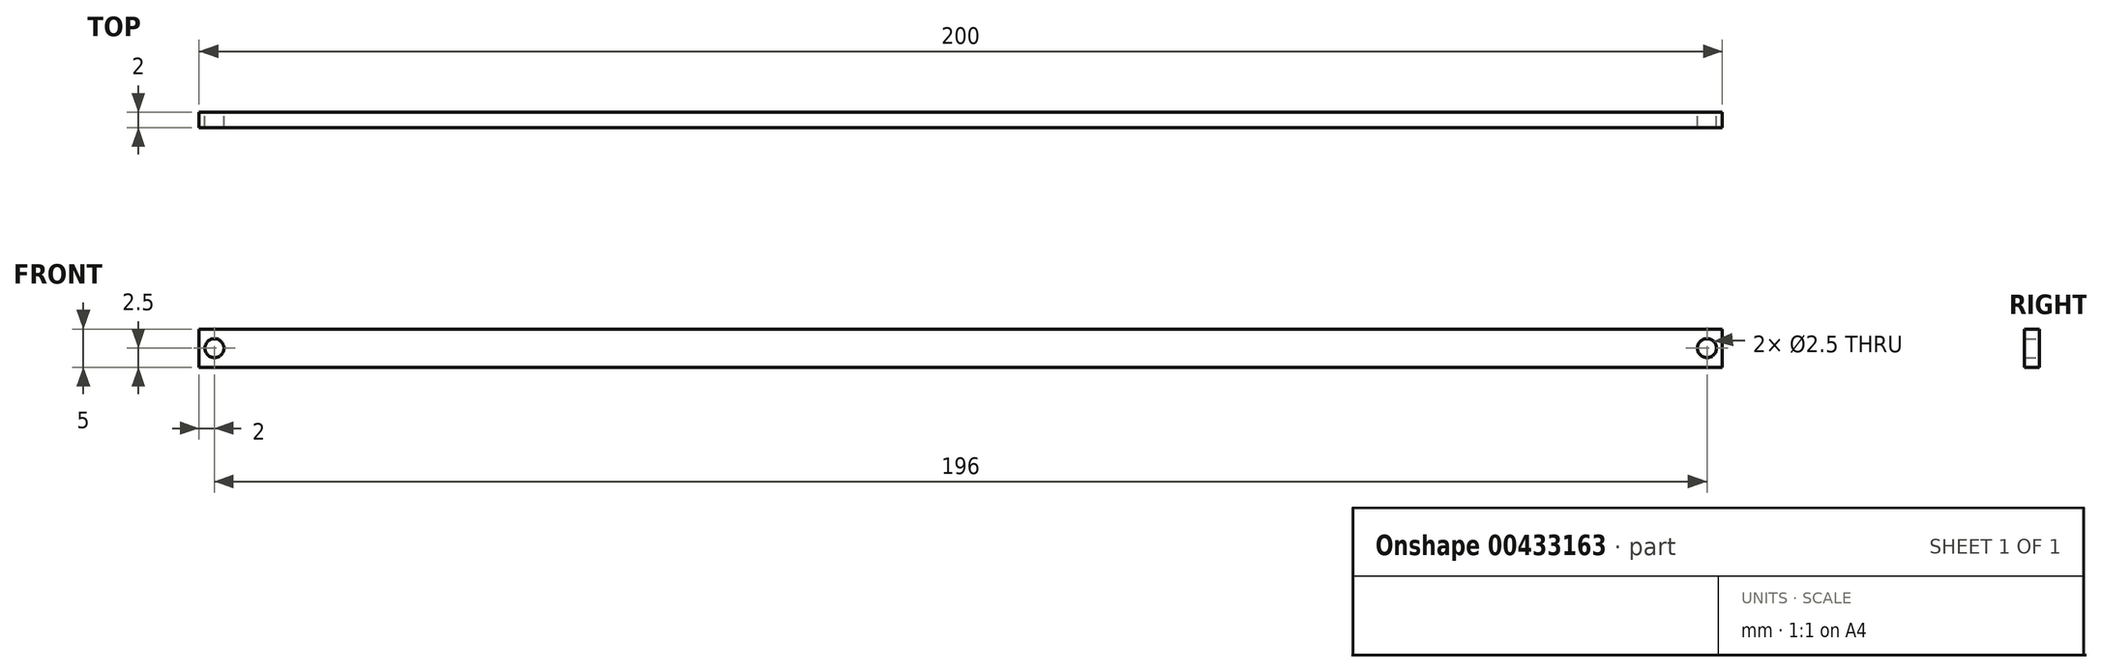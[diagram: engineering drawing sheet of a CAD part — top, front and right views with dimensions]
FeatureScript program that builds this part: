
annotation { "Feature Type Name" : "Feature", "Feature Type Description" : "" }
export const myFeature = defineFeature(function(context is Context, id is Id, definition is map)
    precondition{}
    {
        {
            var Q0;
            Q0=qCreatedBy(makeId("Front.planeOp"),FACE);
            var sketch = newSketch(context, id + "F0", { "sketchPlane" : qUnion([Q0])});
            skLineSegment(sketch, "E0.bottom", {"start": v(-100, 2.5) * mm, "end": v(100, 2.5) * mm});
            skLineSegment(sketch, "E0.top", {"start": v(-100, -2.5) * mm, "end": v(100, -2.5) * mm});
            skLineSegment(sketch, "E0.left", {"start": v(-100, 2.5) * mm, "end": v(-100, -2.5) * mm});
            skLineSegment(sketch, "E0.right", {"start": v(100, 2.5) * mm, "end": v(100, -2.5) * mm});
            skCircle(sketch, "E1", {"center": v(-98, 0) * mm, "radius": 1.25 * mm});
            skCircle(sketch, "E2.MirrorC", {"center": v(98, 0) * mm, "radius": 1.25 * mm});
            skSolve(sketch);
        }
        {
            var Q0;
            Q0 = qSketchRegion(id + "F0", true);
            extrude(context, id + "F1", {"entities" : qUnion([Q0]), "depth" : 2 * mm});
        }
    });
